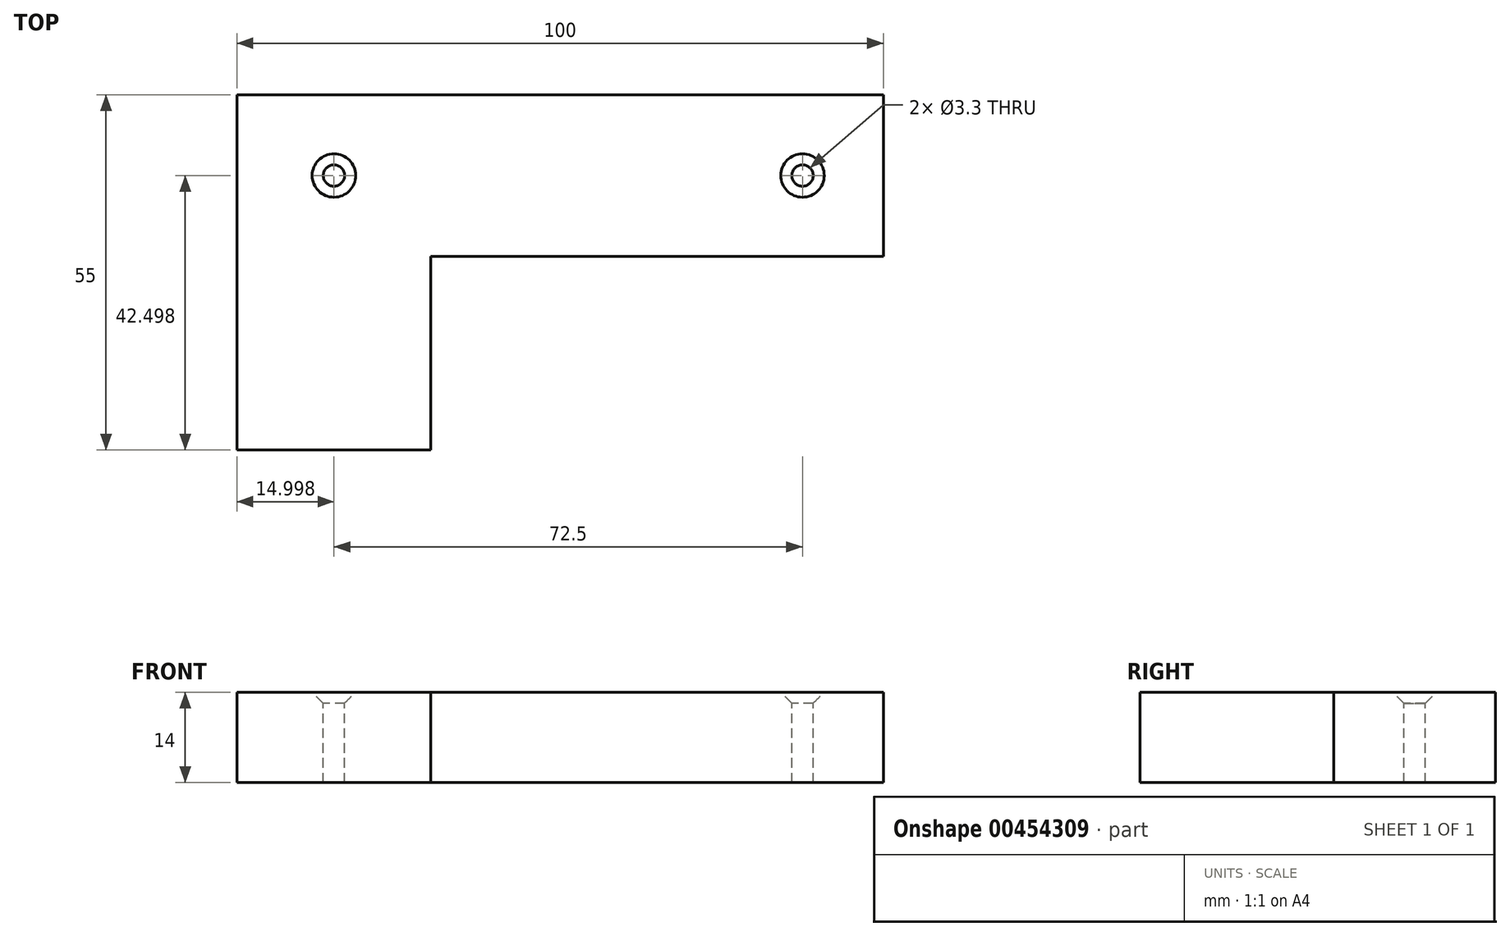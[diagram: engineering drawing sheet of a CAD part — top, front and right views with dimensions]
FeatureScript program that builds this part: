
annotation { "Feature Type Name" : "Feature", "Feature Type Description" : "" }
export const myFeature = defineFeature(function(context is Context, id is Id, definition is map)
    precondition{}
    {
        {
            var Q0;
            Q0=qCreatedBy(makeId("Top.planeOp"),FACE);
            var sketch = newSketch(context, id + "F0", { "sketchPlane" : qUnion([Q0])});
            skLineSegment(sketch, "E0", {"start": v(-54.45, 19.66) * mm, "end": v(-54.45, -35.34) * mm});
            skLineSegment(sketch, "E1", {"start": v(-54.45, 19.66) * mm, "end": v(45.55, 19.66) * mm});
            skLineSegment(sketch, "E2", {"start": v(45.55, 19.66) * mm, "end": v(45.55, -5.34) * mm});
            skLineSegment(sketch, "E3", {"start": v(45.55, -5.34) * mm, "end": v(-24.45, -5.34) * mm});
            skLineSegment(sketch, "E4", {"start": v(-54.45, -35.34) * mm, "end": v(-24.45, -35.34) * mm});
            skLineSegment(sketch, "E5", {"start": v(-24.45, -5.34) * mm, "end": v(-24.45, -35.34) * mm});
            skSolve(sketch);
        }
        {
            var Q0;
            Q0 = qSketchRegion(id + "F0", true);
            extrude(context, id + "F1", {"entities" : qUnion([Q0]), "depth" : 14 * mm});
        }
        {
            var Q0;
            Q0=makeQuery(id+"F1.opExtrude","CAP_FACE",FACE,{"disambiguationData":[OSD([sQuery(id+"F0.wireOp",EDGE,"E0"),sQuery(id+"F0.wireOp",EDGE,"E1"),sQuery(id+"F0.wireOp",EDGE,"E2"),sQuery(id+"F0.wireOp",EDGE,"E3"),sQuery(id+"F0.wireOp",EDGE,"E4"),sQuery(id+"F0.wireOp",EDGE,"E5")])],"isStart":false});
            var sketch = newSketch(context, id + "F2", { "sketchPlane" : qUnion([Q0])});
            skPoint(sketch, "E6", {"position": v(-39.45, 7.16) * mm});
            skPoint(sketch, "E7", {"position": v(33.05, 7.16) * mm});
            skSolve(sketch);
        }
        {
            var Q0;
            Q0=sQuery(id+"F2.wireOp",VERTEX,"E6");
            var Q1;
            Q1=sQuery(id+"F2.wireOp",VERTEX,"E7");
            var Q2;
            Q2=makeQuery(id+"F1.opExtrude","SWEPT_BODY",BODY,{"disambiguationData":[OSD([sQuery(id+"F0.wireOp",EDGE,"E0"),sQuery(id+"F0.wireOp",EDGE,"E1"),sQuery(id+"F0.wireOp",EDGE,"E2"),sQuery(id+"F0.wireOp",EDGE,"E3"),sQuery(id+"F0.wireOp",EDGE,"E4"),sQuery(id+"F0.wireOp",EDGE,"E5")])]});
            hole(context, id + "F3", {"style" : HoleStyle.C_SINK, "endStyle" : HoleEndStyle.THROUGH, "standardTappedOrClearance" : lookupTablePath({ "standard" : "ISO", "fit" : "Normal", "size" : "M3", "type" : "Clearance" }), "standardBlindInLast" : lookupTablePath({ "fit" : "Standard", "standard" : "ISO", "size" : "M3", "type" : "Clearance" }), "holeDiameter" : 3.3 * mm, "cSinkDiameter" : 6.72 * mm, "cSinkAngle" : 90 * degree, "isTappedThrough" : true, "tappedDepth" : 12 * mm, "tapClearance" : 3, "locations" : qUnion([Q0, Q1]), "scope" : qUnion([Q2])});
        }
    });
